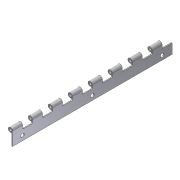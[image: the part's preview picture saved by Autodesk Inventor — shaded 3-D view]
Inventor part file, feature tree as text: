
AUTODESK INVENTOR PART (.ipt)
format: ipt  version: unknown  size: 250,368 bytes
history: native  units: in
note: dims shown in document units (in); Inventor stores cm internally (conversion verified against a paired STEP export)
features: extrude x3, sketch x3, fillet x1, pattern_linear x1, projected_geometry x1
ambient origin geometry x8: Origin, YZ Plane, XZ Plane, XY Plane, X Axis, Y Axis, Z Axis, Center Point
feature tree (9):
  extrude  "Extrusion1"  Depth=0.09in
  extrude  "Extrusion2"  Depth=16.0in TaperAngle=0.0deg
  fillet  "Fillet1"  Radius=1.0in
  pattern_linear  "Rectangular Pattern1"  Spacing1=0.125in  [1 undecoded]
  extrude  "Extrusion3"  Depth=16.0in TaperAngle=0.0deg
  sketch  "Sketch1"  dims[d0=0.445in d1=0.09in]
  sketch  "Sketch2"  dims[d2=0.09in d3=16.0in d4=0.0in d5=1.0in]
  projected_geometry  "Projected Loop1"
  sketch  "Sketch3"  dims[d6=1.0in d7=0.125in d8=16.0in d9=0.0in d10=0.125in d11=3.1496in d13=2.0in d14=0.375in d15=1.0in d16=8.0in d17=1.0in d18=0.375in d19=0.375in d20=1.0in d21=0.0in]
note: 1 required parameter value undecoded (feature->parameter linkage not recoverable at this tier; creation-order binding heuristic only, values carry confidence <= 0.55)
